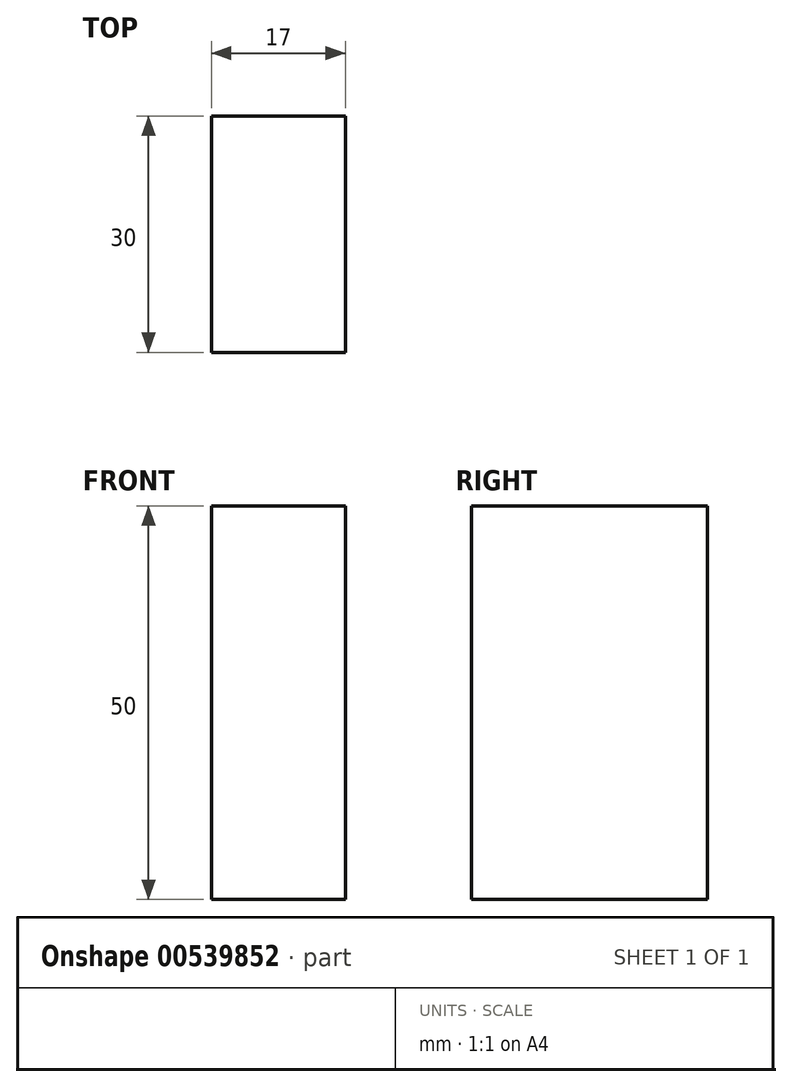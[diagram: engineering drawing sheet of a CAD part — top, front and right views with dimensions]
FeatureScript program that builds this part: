
annotation { "Feature Type Name" : "Feature", "Feature Type Description" : "" }
export const myFeature = defineFeature(function(context is Context, id is Id, definition is map)
    precondition{}
    {
        {
            var Q0;
            Q0=qCreatedBy(makeId("Top.planeOp"),FACE);
            var sketch = newSketch(context, id + "F0", { "sketchPlane" : qUnion([Q0])});
            skLineSegment(sketch, "E0.bottom", {"start": v(8.5, 15) * mm, "end": v(-8.5, 15) * mm});
            skLineSegment(sketch, "E0.top", {"start": v(8.5, -15) * mm, "end": v(-8.5, -15) * mm});
            skLineSegment(sketch, "E0.left", {"start": v(8.5, 15) * mm, "end": v(8.5, -15) * mm});
            skLineSegment(sketch, "E0.right", {"start": v(-8.5, 15) * mm, "end": v(-8.5, -15) * mm});
            skPoint(sketch, "E0.middle", {"position": v(0, 0) * mm});
            skSolve(sketch);
        }
        {
            var Q0;
            Q0=qSketchRegion(id+"F0",true);
            extrude(context, id + "F1", {"entities" : qUnion([Q0]), "depth" : 50 * mm});
        }
    });
